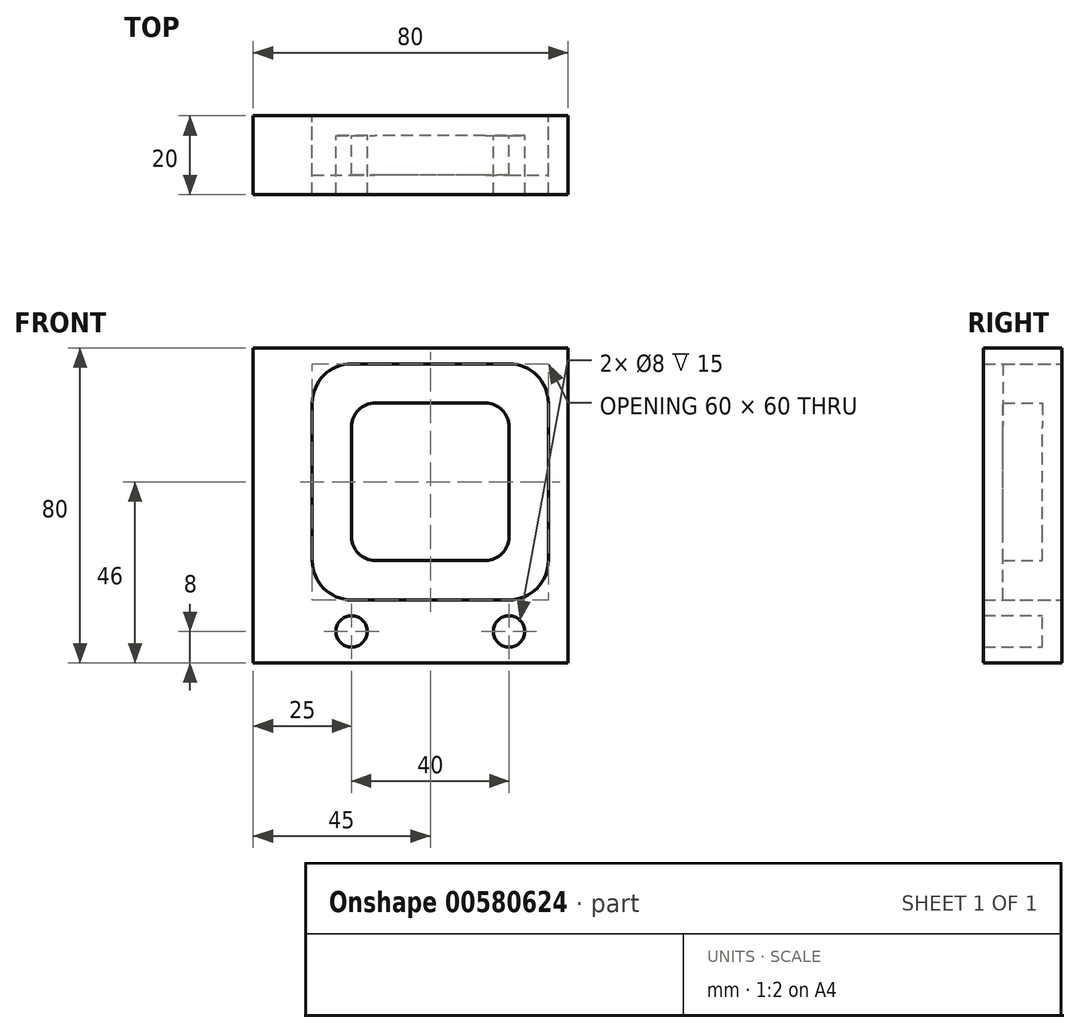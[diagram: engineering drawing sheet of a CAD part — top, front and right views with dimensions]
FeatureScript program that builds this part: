
annotation { "Feature Type Name" : "Feature", "Feature Type Description" : "" }
export const myFeature = defineFeature(function(context is Context, id is Id, definition is map)
    precondition{}
    {
        {
            var Q0;
            Q0=qCreatedBy(makeId("Front.planeOp"),FACE);
            var sketch = newSketch(context, id + "F0", { "sketchPlane" : qUnion([Q0])});
            skLineSegment(sketch, "E0.bottom", {"start": v(20, -30) * mm, "end": v(-20, -30) * mm});
            skLineSegment(sketch, "E0.top", {"start": v(20, 30) * mm, "end": v(-20, 30) * mm});
            skLineSegment(sketch, "E0.left", {"start": v(30, -20) * mm, "end": v(30, 20) * mm});
            skLineSegment(sketch, "E0.right", {"start": v(-30, -20) * mm, "end": v(-30, 20) * mm});
            skPoint(sketch, "E0.middle", {"position": v(0, 0) * mm});
            skPoint(sketch, "E1.visualSharp", {"position": v(30, -30) * mm});
            skArc(sketch, "E1.filletArc", {"start": v(20, -30) * mm, "mid": v(27.07, -27.07) * mm, "end": v(30, -20) * mm});
            skPoint(sketch, "E2.visualSharp", {"position": v(30, 30) * mm});
            skArc(sketch, "E2.filletArc", {"start": v(30, 20) * mm, "mid": v(27.07, 27.07) * mm, "end": v(20, 30) * mm});
            skPoint(sketch, "E3.visualSharp", {"position": v(-30, 30) * mm});
            skArc(sketch, "E3.filletArc", {"start": v(-20, 30) * mm, "mid": v(-27.07, 27.07) * mm, "end": v(-30, 20) * mm});
            skPoint(sketch, "E4.visualSharp", {"position": v(-30, -30) * mm});
            skArc(sketch, "E4.filletArc", {"start": v(-30, -20) * mm, "mid": v(-27.07, -27.07) * mm, "end": v(-20, -30) * mm});
            skLineSegment(sketch, "E5.bottom", {"start": v(35, 34) * mm, "end": v(-45, 34) * mm});
            skLineSegment(sketch, "E5.top", {"start": v(35, -46) * mm, "end": v(-45, -46) * mm});
            skLineSegment(sketch, "E5.left", {"start": v(35, 34) * mm, "end": v(35, -46) * mm});
            skLineSegment(sketch, "E5.right", {"start": v(-45, 34) * mm, "end": v(-45, -46) * mm});
            skCircle(sketch, "E6", {"center": v(20, -38) * mm, "radius": 4 * mm});
            skCircle(sketch, "E7", {"center": v(-20, -38) * mm, "radius": 4 * mm});
            skSolve(sketch);
        }
        {
            var Q0;
            Q0=makeQuery(id+"F0.imprint","IMPRINT",FACE,{"disambiguationData":[TD([[makeQuery(id+"F0.imprint","IMPRINT",EDGE,{"derivedFrom":sQuery(id+"F0.wireOp",EDGE,"E0.bottom")}),1.0]])]});
            extrude(context, id + "F1", {"entities" : qUnion([Q0]), "depth" : 15 * mm, "offsetDistance" : 25 * mm});
        }
        {
            var Q0;
            Q0=makeQuery(id+"F1.opExtrude","CAP_FACE",FACE,{"disambiguationData":[OSD([sQuery(id+"F0.wireOp",EDGE,"E0.bottom"),sQuery(id+"F0.wireOp",EDGE,"E0.top"),sQuery(id+"F0.wireOp",EDGE,"E0.left"),sQuery(id+"F0.wireOp",EDGE,"E0.right"),sQuery(id+"F0.wireOp",EDGE,"E1.filletArc"),sQuery(id+"F0.wireOp",EDGE,"E2.filletArc"),sQuery(id+"F0.wireOp",EDGE,"E3.filletArc"),sQuery(id+"F0.wireOp",EDGE,"E4.filletArc"),sQuery(id+"F0.wireOp",EDGE,"E5.bottom"),sQuery(id+"F0.wireOp",EDGE,"E5.top"),sQuery(id+"F0.wireOp",EDGE,"E5.left"),sQuery(id+"F0.wireOp",EDGE,"E5.right"),sQuery(id+"F0.wireOp",EDGE,"E6"),sQuery(id+"F0.wireOp",EDGE,"E7")])],"isStart":true});
            var sketch = newSketch(context, id + "F2", { "sketchPlane" : qUnion([Q0])});
            skLineSegment(sketch, "E8", {"start": v(-35, -46) * mm, "end": v(-35, 34) * mm});
            skLineSegment(sketch, "E9", {"start": v(-35, 34) * mm, "end": v(45, 34) * mm});
            skLineSegment(sketch, "E10", {"start": v(45, 34) * mm, "end": v(45, -46) * mm});
            skLineSegment(sketch, "E11", {"start": v(45, -46) * mm, "end": v(-35, -46) * mm});
            skLineSegment(sketch, "E12", {"start": v(-20, -30) * mm, "end": v(20, -30) * mm});
            skLineSegment(sketch, "E13", {"start": v(-30, -20) * mm, "end": v(-30, 20) * mm});
            skLineSegment(sketch, "E14", {"start": v(-20, 30) * mm, "end": v(20, 30) * mm});
            skLineSegment(sketch, "E15", {"start": v(30, -20) * mm, "end": v(30, 20) * mm});
            skArc(sketch, "E16", {"start": v(-30, -20) * mm, "mid": v(-27.07, -27.07) * mm, "end": v(-20, -30) * mm});
            skArc(sketch, "E17", {"start": v(20, -30) * mm, "mid": v(27.07, -27.07) * mm, "end": v(30, -20) * mm});
            skArc(sketch, "E18", {"start": v(30, 20) * mm, "mid": v(27.07, 27.07) * mm, "end": v(20, 30) * mm});
            skArc(sketch, "E19", {"start": v(-20, 30) * mm, "mid": v(-27.07, 27.07) * mm, "end": v(-30, 20) * mm});
            skSolve(sketch);
        }
        {
            var Q0;
            Q0 = qSketchRegion(id + "F2", true);
            extrude(context, id + "F3", {"entities" : qUnion([Q0]), "operationType" : NewBodyOperationType.ADD, "depth" : 5 * mm, "offsetDistance" : 25 * mm});
        }
        {
            var Q0;
            Q0=makeQuery(id+"F3.opExtrude","CAP_FACE",FACE,{"disambiguationData":[OSD([sQuery(id+"F2.wireOp",EDGE,"E8"),sQuery(id+"F2.wireOp",EDGE,"E9"),sQuery(id+"F2.wireOp",EDGE,"E10"),sQuery(id+"F2.wireOp",EDGE,"E11"),sQuery(id+"F2.wireOp",EDGE,"E12"),sQuery(id+"F2.wireOp",EDGE,"E13"),sQuery(id+"F2.wireOp",EDGE,"E14"),sQuery(id+"F2.wireOp",EDGE,"E15"),sQuery(id+"F2.wireOp",EDGE,"E16"),sQuery(id+"F2.wireOp",EDGE,"E17"),sQuery(id+"F2.wireOp",EDGE,"E18"),sQuery(id+"F2.wireOp",EDGE,"E19")])],"isStart":false});
            var sketch = newSketch(context, id + "F4", { "sketchPlane" : qUnion([Q0])});
            skLineSegment(sketch, "E20", {"start": v(-20, -30) * mm, "end": v(20, -30) * mm});
            skLineSegment(sketch, "E21", {"start": v(-30, -20) * mm, "end": v(-30, 20) * mm});
            skLineSegment(sketch, "E22", {"start": v(-20, 30) * mm, "end": v(20, 30) * mm});
            skLineSegment(sketch, "E23", {"start": v(30, 20) * mm, "end": v(30, -20) * mm});
            skLineSegment(sketch, "E24.bottom", {"start": v(-14, -20) * mm, "end": v(14, -20) * mm});
            skLineSegment(sketch, "E24.top", {"start": v(-14, 20) * mm, "end": v(14, 20) * mm});
            skLineSegment(sketch, "E24.left", {"start": v(-20, -14) * mm, "end": v(-20, 14) * mm});
            skLineSegment(sketch, "E24.right", {"start": v(20, -14) * mm, "end": v(20, 14) * mm});
            skPoint(sketch, "E24.middle", {"position": v(0, 0) * mm});
            skArc(sketch, "E25", {"start": v(-30, -20) * mm, "mid": v(-27.07, -27.07) * mm, "end": v(-20, -30) * mm});
            skArc(sketch, "E26", {"start": v(20, -30) * mm, "mid": v(27.07, -27.07) * mm, "end": v(30, -20) * mm});
            skArc(sketch, "E27", {"start": v(30, 20) * mm, "mid": v(27.07, 27.07) * mm, "end": v(20, 30) * mm});
            skArc(sketch, "E28", {"start": v(-20, 30) * mm, "mid": v(-27.07, 27.07) * mm, "end": v(-30, 20) * mm});
            skArc(sketch, "E29.filletArc", {"start": v(-20, -14) * mm, "mid": v(-18.24, -18.24) * mm, "end": v(-14, -20) * mm});
            skArc(sketch, "E30.filletArc", {"start": v(-14, 20) * mm, "mid": v(-18.24, 18.24) * mm, "end": v(-20, 14) * mm});
            skArc(sketch, "E31.filletArc", {"start": v(20, 14) * mm, "mid": v(18.24, 18.24) * mm, "end": v(14, 20) * mm});
            skArc(sketch, "E32.filletArc", {"start": v(14, -20) * mm, "mid": v(18.24, -18.24) * mm, "end": v(20, -14) * mm});
            skSolve(sketch);
        }
        {
            var Q0;
            Q0=makeQuery(id+"F4.imprint","IMPRINT",FACE,{"disambiguationData":[TD([[makeQuery(id+"F4.imprint","IMPRINT",EDGE,{"derivedFrom":sQuery(id+"F4.wireOp",EDGE,"E20")}),1.0]])]});
            extrude(context, id + "F5", {"entities" : qUnion([Q0]), "oppositeDirection" : true, "depth" : 15 * mm, "offsetDistance" : 25 * mm});
        }
        {
            var Q0;
            Q0=makeQuery(id+"F5.opExtrude","CAP_FACE",FACE,{"disambiguationData":[OSD([sQuery(id+"F4.wireOp",EDGE,"E20"),sQuery(id+"F4.wireOp",EDGE,"E21"),sQuery(id+"F4.wireOp",EDGE,"E22"),sQuery(id+"F4.wireOp",EDGE,"E23"),sQuery(id+"F4.wireOp",EDGE,"E24.bottom"),sQuery(id+"F4.wireOp",EDGE,"E24.top"),sQuery(id+"F4.wireOp",EDGE,"E24.left"),sQuery(id+"F4.wireOp",EDGE,"E24.right"),sQuery(id+"F4.wireOp",EDGE,"E25"),sQuery(id+"F4.wireOp",EDGE,"E26"),sQuery(id+"F4.wireOp",EDGE,"E27"),sQuery(id+"F4.wireOp",EDGE,"E28"),sQuery(id+"F4.wireOp",EDGE,"E29.filletArc"),sQuery(id+"F4.wireOp",EDGE,"E30.filletArc"),sQuery(id+"F4.wireOp",EDGE,"E31.filletArc"),sQuery(id+"F4.wireOp",EDGE,"E32.filletArc")])],"isStart":true});
            var sketch = newSketch(context, id + "F6", { "sketchPlane" : qUnion([Q0])});
            skLineSegment(sketch, "E33", {"start": v(-14, -20) * mm, "end": v(14, -20) * mm});
            skLineSegment(sketch, "E34", {"start": v(20, -14) * mm, "end": v(20, 14) * mm});
            skLineSegment(sketch, "E35", {"start": v(-14, 20) * mm, "end": v(14, 20) * mm});
            skLineSegment(sketch, "E36", {"start": v(-20, -14) * mm, "end": v(-20, 14) * mm});
            skArc(sketch, "E37", {"start": v(-20, -14) * mm, "mid": v(-18.24, -18.24) * mm, "end": v(-14, -20) * mm});
            skArc(sketch, "E38", {"start": v(14, -20) * mm, "mid": v(18.24, -18.24) * mm, "end": v(20, -14) * mm});
            skArc(sketch, "E39", {"start": v(20, 14) * mm, "mid": v(18.24, 18.24) * mm, "end": v(14, 20) * mm});
            skArc(sketch, "E40", {"start": v(-14, 20) * mm, "mid": v(-18.24, 18.24) * mm, "end": v(-20, 14) * mm});
            skSolve(sketch);
        }
        {
            var Q0;
            Q0=makeQuery(id+"F6.imprint","IMPRINT",FACE,{"disambiguationData":[TD([[makeQuery(id+"F6.imprint","IMPRINT",EDGE,{"derivedFrom":sQuery(id+"F6.wireOp",EDGE,"E33")}),1.0]])]});
            extrude(context, id + "F7", {"entities" : qUnion([Q0]), "operationType" : NewBodyOperationType.ADD, "oppositeDirection" : true, "depth" : 5 * mm, "offsetDistance" : 25 * mm});
        }
    });
